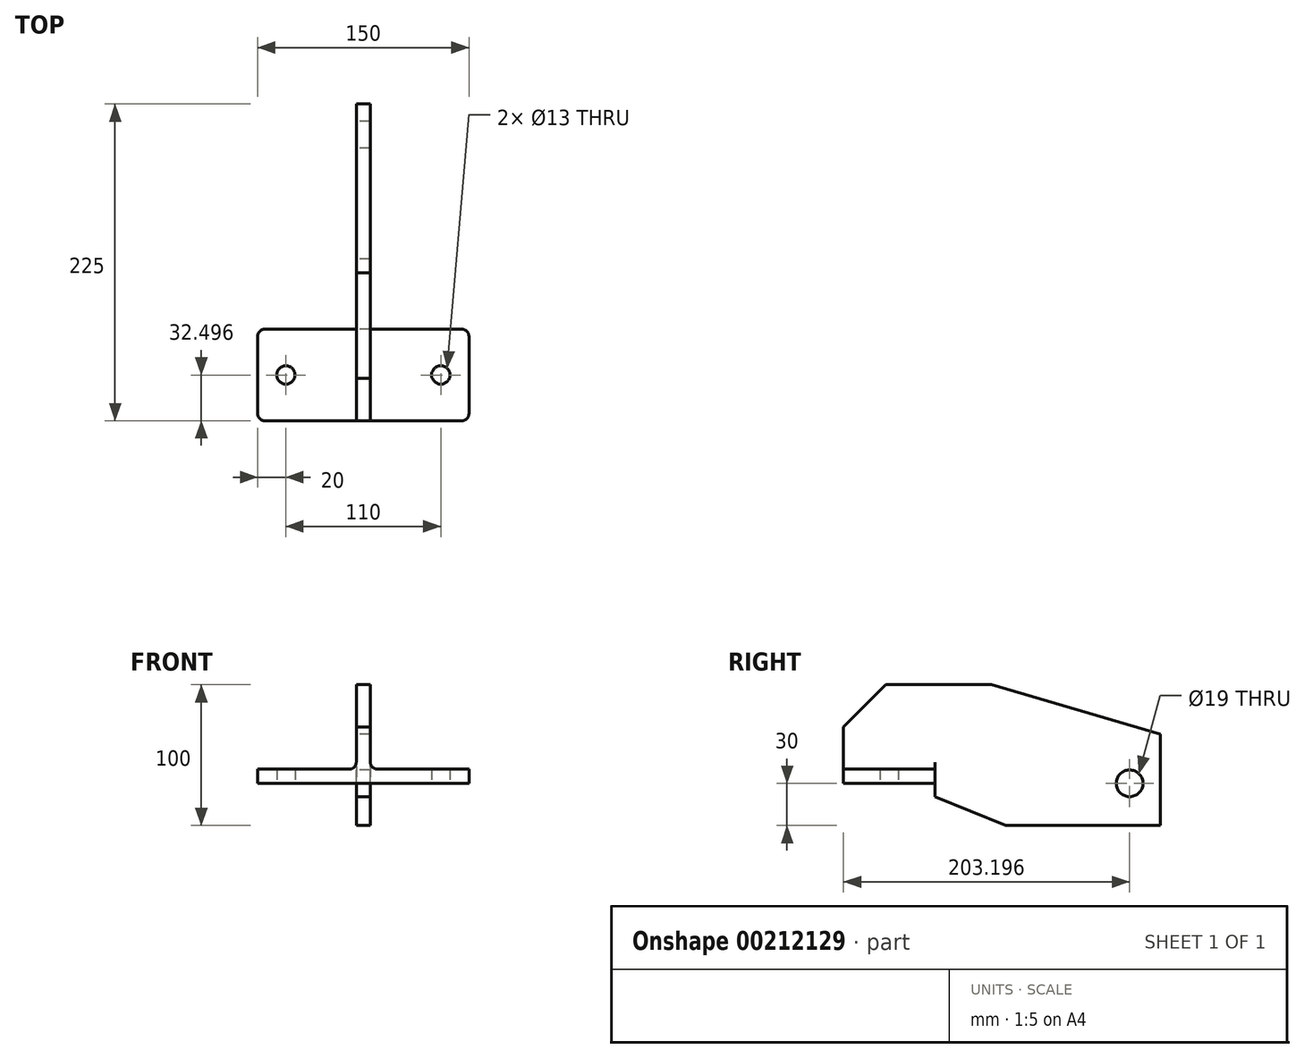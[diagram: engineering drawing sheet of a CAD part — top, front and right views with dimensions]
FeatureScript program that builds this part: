
annotation { "Feature Type Name" : "Feature", "Feature Type Description" : "" }
export const myFeature = defineFeature(function(context is Context, id is Id, definition is map)
    precondition{}
    {
        {
            var Q0;
            Q0=qCreatedBy(makeId("Right.planeOp"),FACE);
            var sketch = newSketch(context, id + "F0", { "sketchPlane" : qUnion([Q0])});
            skLineSegment(sketch, "E0", {"start": v(-115.66, -14.6) * mm, "end": v(-115.66, 25.4) * mm});
            skLineSegment(sketch, "E1", {"start": v(-115.66, 25.4) * mm, "end": v(-85.66, 55.4) * mm});
            skLineSegment(sketch, "E2", {"start": v(-85.66, 55.4) * mm, "end": v(-10.66, 55.4) * mm});
            skLineSegment(sketch, "E3", {"start": v(-10.66, 55.4) * mm, "end": v(109.34, 20.4) * mm});
            skLineSegment(sketch, "E4", {"start": v(109.34, 20.4) * mm, "end": v(109.34, -44.6) * mm});
            skLineSegment(sketch, "E5", {"start": v(109.34, -44.6) * mm, "end": v(-0.66, -44.6) * mm});
            skLineSegment(sketch, "E6", {"start": v(-115.66, -14.6) * mm, "end": v(-50.66, -14.6) * mm});
            skLineSegment(sketch, "E7", {"start": v(-50.66, -14.6) * mm, "end": v(-50.66, -24.13) * mm});
            skLineSegment(sketch, "E8", {"start": v(-50.66, -24.13) * mm, "end": v(-0.66, -44.6) * mm});
            skPoint(sketch, "E9", {"position": v(87.54, -14.6) * mm});
            skCircle(sketch, "E10", {"center": v(87.54, -14.6) * mm, "radius": 9.5 * mm});
            skLineSegment(sketch, "E11", {"start": v(-50.66, -14.6) * mm, "end": v(87.54, -14.6) * mm, "construction": true});
            skSolve(sketch);
        }
        {
            var Q0;
            Q0=makeQuery(id+"F0.imprint","IMPRINT",FACE,{"disambiguationData":[TD([[makeQuery(id+"F0.imprint","IMPRINT",EDGE,{"derivedFrom":sQuery(id+"F0.wireOp",EDGE,"E0")}),-1.0]])]});
            extrude(context, id + "F1", {"entities" : qUnion([Q0]), "endBound" : BoundingType.SYMMETRIC, "depth" : 10 * mm});
        }
        {
            var Q0;
            Q0=makeQuery(id+"F1.opExtrude","SWEPT_FACE",FACE,{"disambiguationData":[OSD([sQuery(id+"F0.wireOp",EDGE,"E6")])]});
            var sketch = newSketch(context, id + "F2", { "sketchPlane" : qUnion([Q0])});
            skPoint(sketch, "E12.endSnap0", {"position": v(-5, 83.16) * mm});
            skPoint(sketch, "E13.visualSharp", {"position": v(75, 39.46) * mm});
            skPoint(sketch, "E14.visualSharp", {"position": v(75, 115.66) * mm});
            skPoint(sketch, "E15.0", {"position": v(0, 50.66) * mm});
            skPoint(sketch, "E16.0", {"position": v(0, 115.66) * mm});
            skLineSegment(sketch, "E17", {"start": v(0, 50.66) * mm, "end": v(0, 83.16) * mm, "construction": true});
            skLineSegment(sketch, "E18.bottom", {"start": v(-70, 50.66) * mm, "end": v(70, 50.66) * mm});
            skLineSegment(sketch, "E18.top", {"start": v(-70, 115.66) * mm, "end": v(70, 115.66) * mm});
            skLineSegment(sketch, "E18.left", {"start": v(-75, 55.66) * mm, "end": v(-75, 110.66) * mm});
            skLineSegment(sketch, "E18.right", {"start": v(75, 55.66) * mm, "end": v(75, 110.66) * mm});
            skPoint(sketch, "E18.middle", {"position": v(0, 83.16) * mm});
            skLineSegment(sketch, "E19", {"start": v(0, 83.16) * mm, "end": v(55, 83.16) * mm, "construction": true});
            skCircle(sketch, "E20", {"center": v(55, 83.16) * mm, "radius": 6.5 * mm});
            skCircle(sketch, "E21.MirrorC", {"center": v(-55, 83.16) * mm, "radius": 6.5 * mm});
            skArc(sketch, "E22.filletArc", {"start": v(75, 110.66) * mm, "mid": v(73.54, 114.2) * mm, "end": v(70, 115.66) * mm});
            skPoint(sketch, "E23.visualSharp", {"position": v(75, 50.66) * mm});
            skArc(sketch, "E23.filletArc", {"start": v(70, 50.66) * mm, "mid": v(73.54, 52.13) * mm, "end": v(75, 55.66) * mm});
            skPoint(sketch, "E24.visualSharp", {"position": v(-75, 50.66) * mm});
            skArc(sketch, "E24.filletArc", {"start": v(-75, 55.66) * mm, "mid": v(-73.54, 52.13) * mm, "end": v(-70, 50.66) * mm});
            skPoint(sketch, "E25.visualSharp", {"position": v(-75, 115.66) * mm});
            skArc(sketch, "E25.filletArc", {"start": v(-70, 115.66) * mm, "mid": v(-73.54, 114.2) * mm, "end": v(-75, 110.66) * mm});
            skSolve(sketch);
        }
        {
            var Q0;
            Q0=makeQuery(id+"F2.imprint","IMPRINT",FACE,{"disambiguationData":[TD([[makeQuery(id+"F2.imprint","IMPRINT",EDGE,{"derivedFrom":sQuery(id+"F2.wireOp",EDGE,"E18.left")}),-1.0]])]});
            var Q1;
            {var subQ1=sQuery(id+"F0.wireOp",EDGE,"E6");var subQ2=makeQuery(id+"F1.opExtrude","CAP_EDGE",EDGE,{"disambiguationData":[OSD([subQ1])],"isStart":true});Q1=makeQuery(id+"F2.imprint","IMPRINT",FACE,{"disambiguationData":[TD([[makeQuery(id+"F2.imprint","IMPRINT",EDGE,{"derivedFrom":subQ2}),1.0]])]});}
            var Q2;
            Q2=makeQuery(id+"F2.imprint","IMPRINT",FACE,{"disambiguationData":[TD([[makeQuery(id+"F2.imprint","IMPRINT",EDGE,{"derivedFrom":sQuery(id+"F2.wireOp",EDGE,"E18.right")}),1.0]])]});
            extrude(context, id + "F3", {"entities" : qUnion([Q0, Q1, Q2]), "operationType" : NewBodyOperationType.ADD, "oppositeDirection" : true, "depth" : 10 * mm});
        }
        {
            var Q0;
            Q0=makeQuery(id+"F3.boolean.opBoolean","INTERSECT",EDGE,{"derivedFrom":[makeQuery(id+"F1.opExtrude","CAP_FACE",FACE,{"disambiguationData":[OSD([sQuery(id+"F0.wireOp",EDGE,"E0"),sQuery(id+"F0.wireOp",EDGE,"E1"),sQuery(id+"F0.wireOp",EDGE,"E2"),sQuery(id+"F0.wireOp",EDGE,"E3"),sQuery(id+"F0.wireOp",EDGE,"E4"),sQuery(id+"F0.wireOp",EDGE,"E5"),sQuery(id+"F0.wireOp",EDGE,"E6"),sQuery(id+"F0.wireOp",EDGE,"E7"),sQuery(id+"F0.wireOp",EDGE,"E8"),sQuery(id+"F0.wireOp",EDGE,"E10")])],"isStart":false}),makeQuery(id+"F3.opExtrude","CAP_FACE",FACE,{"disambiguationData":[OSD([sQuery(id+"F2.wireOp",EDGE,"E18.bottom"),sQuery(id+"F2.wireOp",EDGE,"E18.top"),sQuery(id+"F2.wireOp",EDGE,"E18.left"),sQuery(id+"F2.wireOp",EDGE,"E18.right"),sQuery(id+"F2.wireOp",EDGE,"E20"),sQuery(id+"F2.wireOp",EDGE,"E21.MirrorC"),sQuery(id+"F2.wireOp",EDGE,"E22.filletArc"),sQuery(id+"F2.wireOp",EDGE,"E23.filletArc"),sQuery(id+"F2.wireOp",EDGE,"E24.filletArc"),sQuery(id+"F2.wireOp",EDGE,"E25.filletArc")])],"isStart":false})]});
            var Q1;
            Q1=makeQuery(id+"F3.boolean.opBoolean","INTERSECT",EDGE,{"derivedFrom":[makeQuery(id+"F1.opExtrude","CAP_FACE",FACE,{"disambiguationData":[OSD([sQuery(id+"F0.wireOp",EDGE,"E0"),sQuery(id+"F0.wireOp",EDGE,"E1"),sQuery(id+"F0.wireOp",EDGE,"E2"),sQuery(id+"F0.wireOp",EDGE,"E3"),sQuery(id+"F0.wireOp",EDGE,"E4"),sQuery(id+"F0.wireOp",EDGE,"E5"),sQuery(id+"F0.wireOp",EDGE,"E6"),sQuery(id+"F0.wireOp",EDGE,"E7"),sQuery(id+"F0.wireOp",EDGE,"E8"),sQuery(id+"F0.wireOp",EDGE,"E10")])],"isStart":true}),makeQuery(id+"F3.opExtrude","CAP_FACE",FACE,{"disambiguationData":[OSD([sQuery(id+"F2.wireOp",EDGE,"E18.bottom"),sQuery(id+"F2.wireOp",EDGE,"E18.top"),sQuery(id+"F2.wireOp",EDGE,"E18.left"),sQuery(id+"F2.wireOp",EDGE,"E18.right"),sQuery(id+"F2.wireOp",EDGE,"E20"),sQuery(id+"F2.wireOp",EDGE,"E21.MirrorC"),sQuery(id+"F2.wireOp",EDGE,"E22.filletArc"),sQuery(id+"F2.wireOp",EDGE,"E23.filletArc"),sQuery(id+"F2.wireOp",EDGE,"E24.filletArc"),sQuery(id+"F2.wireOp",EDGE,"E25.filletArc")])],"isStart":false})]});
            fillet(context, id + "F4", {"entities" : qUnion([Q0, Q1]), "radius" : 5 * mm, "tangentPropagation" : true, "allowEdgeOverflow" : false});
        }
    });
